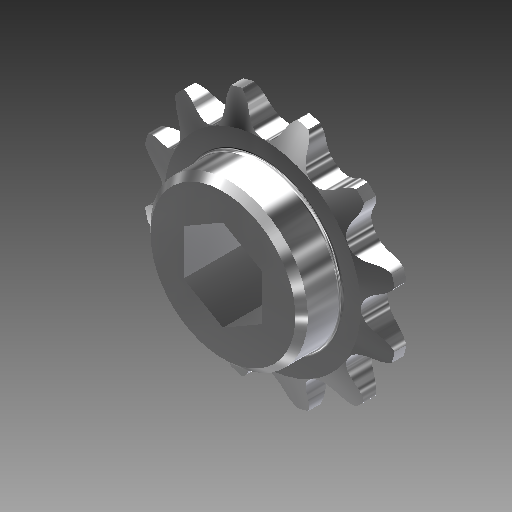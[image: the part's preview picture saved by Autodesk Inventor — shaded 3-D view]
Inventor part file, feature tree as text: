
AUTODESK INVENTOR PART (.ipt)
format: ipt  version: 2019 (Build 230136000, 136)  size: 510,464 bytes
history: native  units: in
note: dims shown in document units (in); Inventor stores cm internally (conversion verified against a paired STEP export)
features: chamfer x1, other x1, imported_body x1
ambient origin geometry x8: Origin, YZ Plane, XZ Plane, XY Plane, X Axis, Y Axis, Z Axis, Center Point
bodies: Body1 (feature_tree)
feature tree (3):
  chamfer  "Chamfer1"  [1 undecoded]
  other  "Sprocket 35_12T1"
  imported_body  "Base1"
note: 1 required parameter value undecoded (feature->parameter linkage not recoverable at this tier; creation-order binding heuristic only, values carry confidence <= 0.55)
